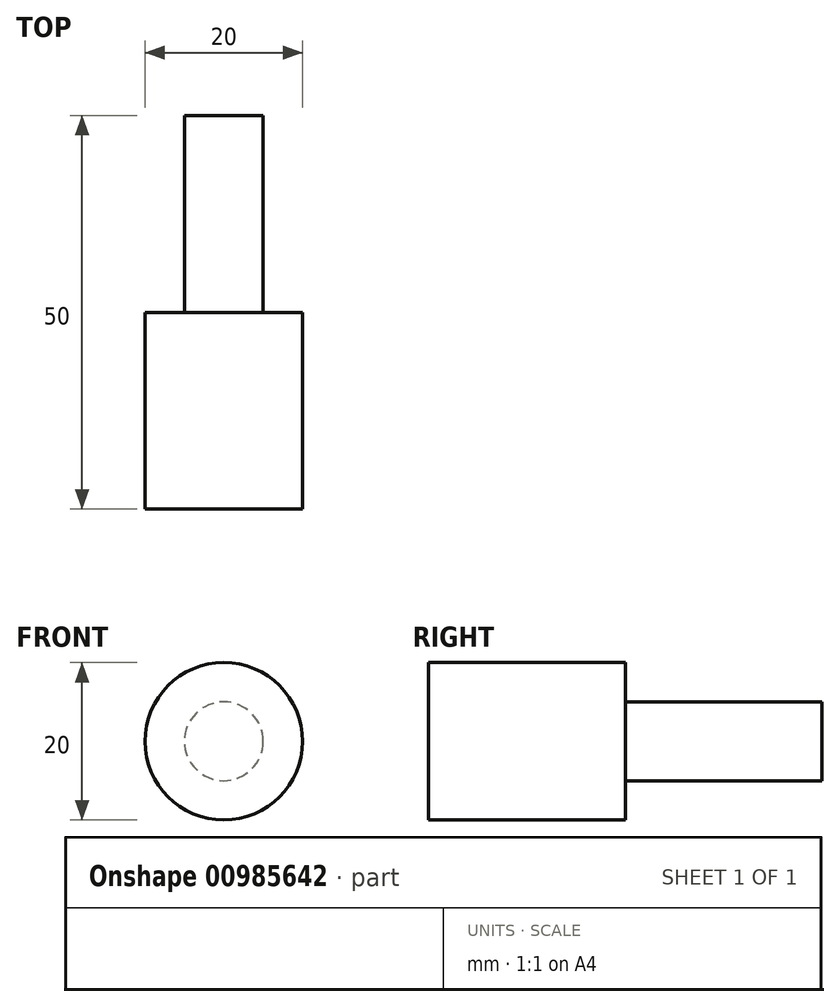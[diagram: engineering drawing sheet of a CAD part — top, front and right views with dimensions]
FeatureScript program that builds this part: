
annotation { "Feature Type Name" : "Feature", "Feature Type Description" : "" }
export const myFeature = defineFeature(function(context is Context, id is Id, definition is map)
    precondition{}
    {
        {
            var Q0;
            Q0=qCreatedBy(makeId("Front.planeOp"),FACE);
            var sketch = newSketch(context, id + "F0", { "sketchPlane" : qUnion([Q0])});
            skCircle(sketch, "E0.0", {"center": v(0, 0) * mm, "radius": 5 * mm, "construction": true});
            skCircle(sketch, "E1.0", {"center": v(0, 0) * mm, "radius": 10 * mm});
            skSolve(sketch);
        }
        {
            var Q0;
            Q0 = qSketchRegion(id + "F0", true);
            extrude(context, id + "F1", {"entities" : qUnion([Q0]), "depth" : 25 * mm, "offsetDistance" : 25 * mm});
        }
        {
            var Q0;
            Q0=makeQuery(id+"F0.imprint","IMPRINT",FACE,{"disambiguationData":[TD([[makeQuery(id+"F0.imprint","IMPRINT",EDGE,{"derivedFrom":sQuery(id+"F0.wireOp",EDGE,"E1.0")}),1.0]])]});
            var sketch = newSketch(context, id + "F2", { "sketchPlane" : qUnion([Q0])});
            skCircle(sketch, "E2.0", {"center": v(0, 0) * mm, "radius": 5 * mm});
            skSolve(sketch);
        }
        {
            var Q0;
            Q0=makeQuery(id+"F2.imprint","IMPRINT",FACE,{"disambiguationData":[TD([[makeQuery(id+"F2.imprint","IMPRINT",EDGE,{"derivedFrom":sQuery(id+"F2.wireOp",EDGE,"E2.0")}),1.0]])]});
            var Q1;
            Q1=sQuery(id+"F2.wireOp",EDGE,"E2.0");
            extrude(context, id + "F3", {"entities" : qUnion([Q0]), "surfaceEntities" : qUnion([Q1]), "oppositeDirection" : true, "depth" : 25 * mm, "offsetDistance" : 25 * mm});
        }
    });
